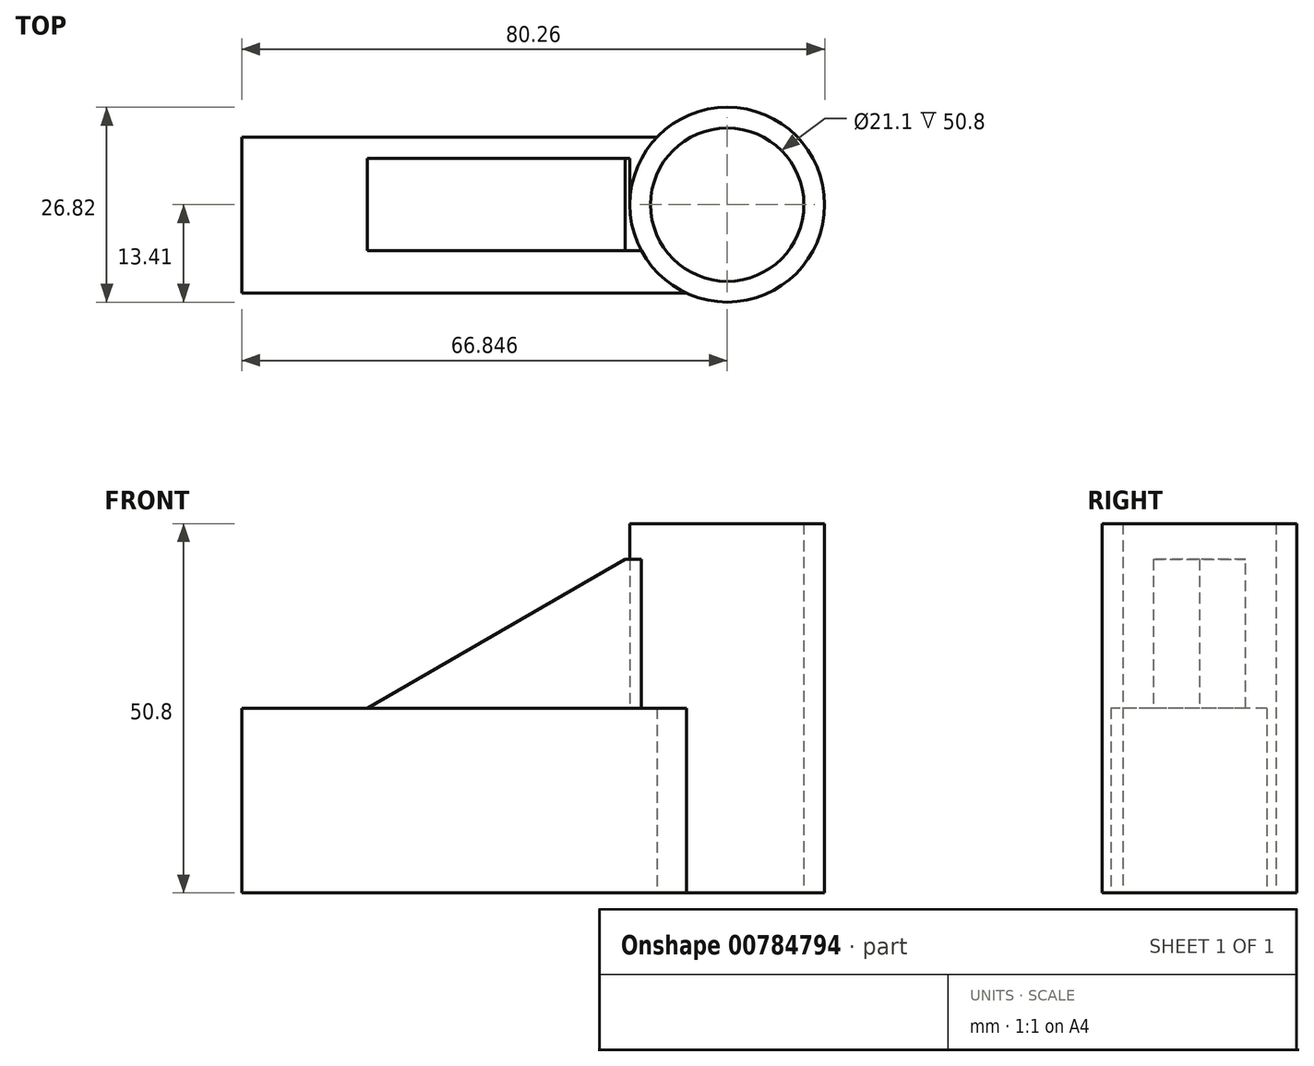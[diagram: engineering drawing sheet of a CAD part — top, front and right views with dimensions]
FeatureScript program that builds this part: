
annotation { "Feature Type Name" : "Feature", "Feature Type Description" : "" }
export const myFeature = defineFeature(function(context is Context, id is Id, definition is map)
    precondition{}
    {
        {
            var Q0;
            Q0=qCreatedBy(makeId("Top.planeOp"),FACE);
            var sketch = newSketch(context, id + "F0", { "sketchPlane" : qUnion([Q0])});
            skLineSegment(sketch, "E0.bottom", {"start": v(-59.16, 9.28) * mm, "end": v(-4.46, 9.28) * mm});
            skLineSegment(sketch, "E0.top", {"start": v(-59.16, -12.17) * mm, "end": v(-4.46, -12.17) * mm});
            skLineSegment(sketch, "E0.left", {"start": v(-59.16, 9.28) * mm, "end": v(-59.16, -12.17) * mm});
            skCircle(sketch, "E1", {"center": v(7.69, 0) * mm, "radius": 13.41 * mm});
            skLineSegment(sketch, "E2", {"start": v(-4.46, 9.28) * mm, "end": v(-2, 9.28) * mm});
            skLineSegment(sketch, "E3", {"start": v(-4.46, -12.17) * mm, "end": v(2.05, -12.17) * mm});
            skCircle(sketch, "E4", {"center": v(7.69, 0) * mm, "radius": 10.55 * mm});
            skSolve(sketch);
        }
        {
            var Q0;
            Q0=makeQuery(id+"F0.imprint","IMPRINT",FACE,{"disambiguationData":[TD([[makeQuery(id+"F0.imprint","IMPRINT",EDGE,{"derivedFrom":sQuery(id+"F0.wireOp",EDGE,"E0.bottom")}),-1.0]])]});
            extrude(context, id + "F1", {"entities" : qUnion([Q0]), "depth" : 25.4 * mm, "offsetDistance" : 25.4 * mm});
        }
        {
            var Q0;
            Q0=makeQuery(id+"F0.imprint","IMPRINT",FACE,{"disambiguationData":[TD([[makeQuery(id+"F0.imprint","IMPRINT",EDGE,{"derivedFrom":sQuery(id+"F0.wireOp",EDGE,"E4")}),-1.0]])]});
            extrude(context, id + "F2", {"entities" : qUnion([Q0]), "operationType" : NewBodyOperationType.ADD, "depth" : 50.8 * mm, "offsetDistance" : 25.4 * mm});
        }
        {
            var Q0;
            Q0=qCreatedBy(makeId("Front.planeOp"),FACE);
            var sketch = newSketch(context, id + "F3", { "sketchPlane" : qUnion([Q0])});
            skLineSegment(sketch, "E5", {"start": v(-43.5, 24.46) * mm, "end": v(-6.39, 45.9) * mm});
            skLineSegment(sketch, "E6", {"start": v(-6.39, 45.9) * mm, "end": v(-6.39, 23.01) * mm});
            skLineSegment(sketch, "E7", {"start": v(-6.39, 23.01) * mm, "end": v(-43.5, 23.01) * mm});
            skLineSegment(sketch, "E8", {"start": v(-43.5, 23.01) * mm, "end": v(-43.5, 24.46) * mm});
            skSolve(sketch);
        }
        {
            var Q0;
            Q0=makeQuery(id+"F3.imprint","IMPRINT",FACE,{"disambiguationData":[TD([[makeQuery(id+"F3.imprint","IMPRINT",EDGE,{"derivedFrom":sQuery(id+"F3.wireOp",EDGE,"E5")}),-1.0]])]});
            extrude(context, id + "F4", {"entities" : qUnion([Q0]), "operationType" : NewBodyOperationType.ADD, "depth" : 6.35 * mm, "offsetDistance" : 25.4 * mm});
        }
        {
            var Q0;
            Q0=makeQuery(id+"F4.opExtrude","SWEPT_FACE",FACE,{"disambiguationData":[OSD([sQuery(id+"F3.wireOp",EDGE,"E6")])]});
            extrude(context, id + "F5", {"entities" : qUnion([Q0]), "operationType" : NewBodyOperationType.ADD, "depth" : 2.54 * mm, "offsetDistance" : 25.4 * mm});
        }
        {
            var Q0;
            {var subQ0=sQuery(id+"F3.wireOp",EDGE,"E6");Q0=makeQuery(id+"F5.boolean.opBoolean","MERGE",FACE,{"derivedFrom":[makeQuery(id+"F4.opExtrude","CAP_FACE",FACE,{"disambiguationData":[OSD([sQuery(id+"F3.wireOp",EDGE,"E5"),subQ0,sQuery(id+"F3.wireOp",EDGE,"E7"),sQuery(id+"F3.wireOp",EDGE,"E8")])],"isStart":true}),makeQuery(id+"F5.opExtrude","SWEPT_FACE",FACE,{"disambiguationData":[OSD([subQ0]),TDD([makeQuery(id+"F4.opExtrude","CAP_EDGE",EDGE,{"disambiguationData":[OSD([subQ0])],"isStart":true})])]})]});}
            extrude(context, id + "F6", {"entities" : qUnion([Q0]), "operationType" : NewBodyOperationType.ADD, "depth" : 6.35 * mm, "offsetDistance" : 25.4 * mm});
        }
    });
